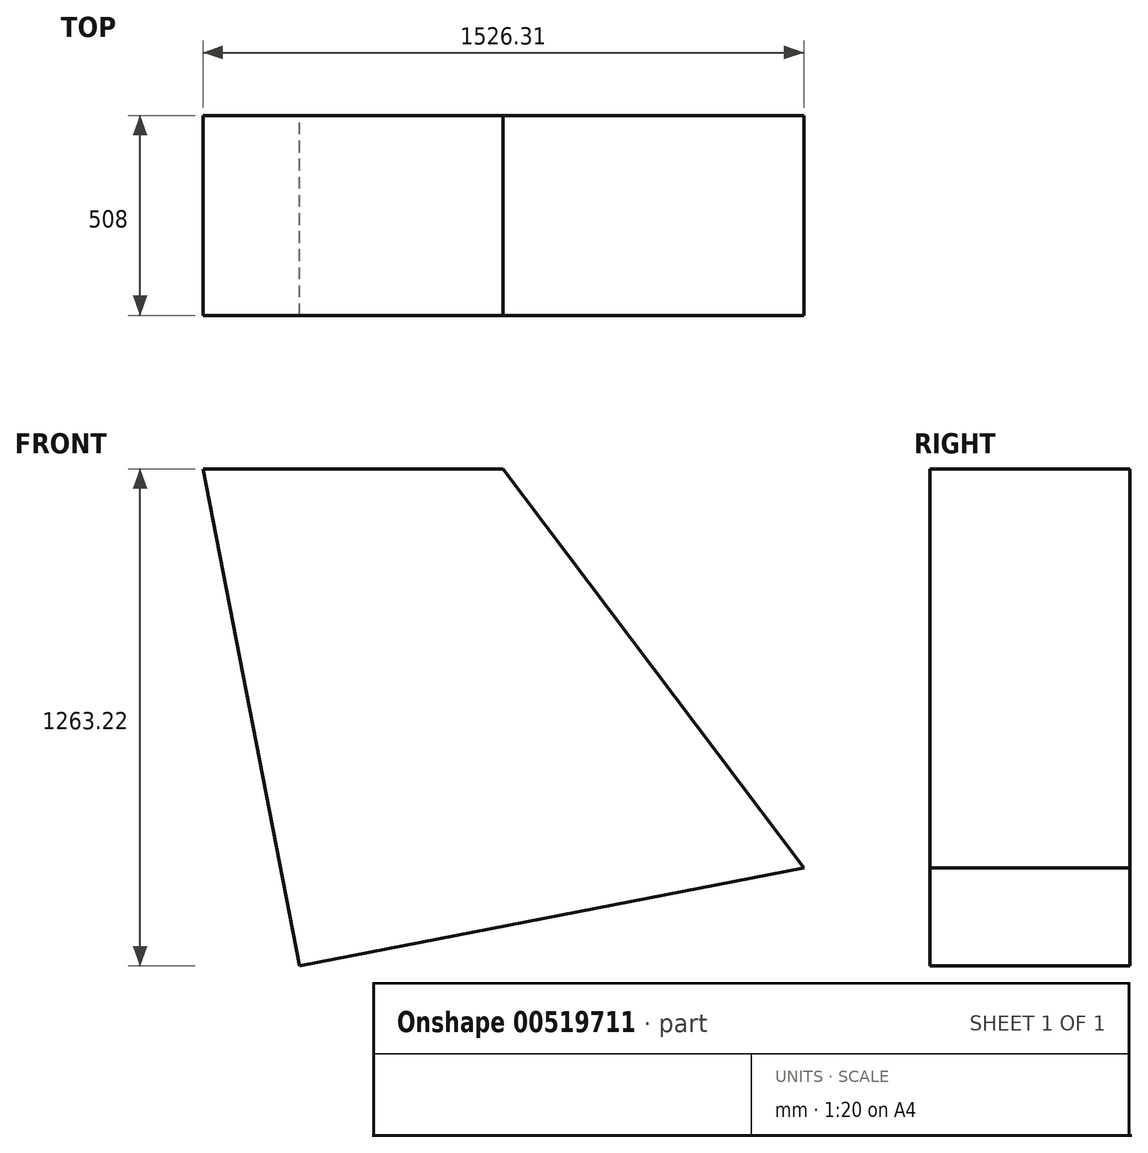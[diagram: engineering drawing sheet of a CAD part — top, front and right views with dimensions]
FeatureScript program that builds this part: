
annotation { "Feature Type Name" : "Feature", "Feature Type Description" : "" }
export const myFeature = defineFeature(function(context is Context, id is Id, definition is map)
    precondition{}
    {
        {
            var Q0;
            Q0=qCreatedBy(makeId("Front.planeOp"),FACE);
            var sketch = newSketch(context, id + "F0", { "sketchPlane" : qUnion([Q0])});
            skLineSegment(sketch, "E0", {"start": v(-523.88, 606.58) * mm, "end": v(238.12, 606.58) * mm});
            skLineSegment(sketch, "E1", {"start": v(238.12, 606.58) * mm, "end": v(1002.43, -407.69) * mm});
            skLineSegment(sketch, "E2", {"start": v(1002.43, -407.69) * mm, "end": v(-278.33, -656.64) * mm});
            skLineSegment(sketch, "E3", {"start": v(-278.33, -656.64) * mm, "end": v(-523.88, 606.58) * mm});
            skSolve(sketch);
        }
        {
            var Q0;
            Q0=makeQuery(id+"F0.imprint","IMPRINT",FACE,{"disambiguationData":[TD([[makeQuery(id+"F0.imprint","IMPRINT",EDGE,{"derivedFrom":sQuery(id+"F0.wireOp",EDGE,"E0")}),-1.0]])]});
            extrude(context, id + "F1", {"entities" : qUnion([Q0]), "depth" : 508 * mm, "offsetDistance" : 25.4 * mm});
        }
    });
